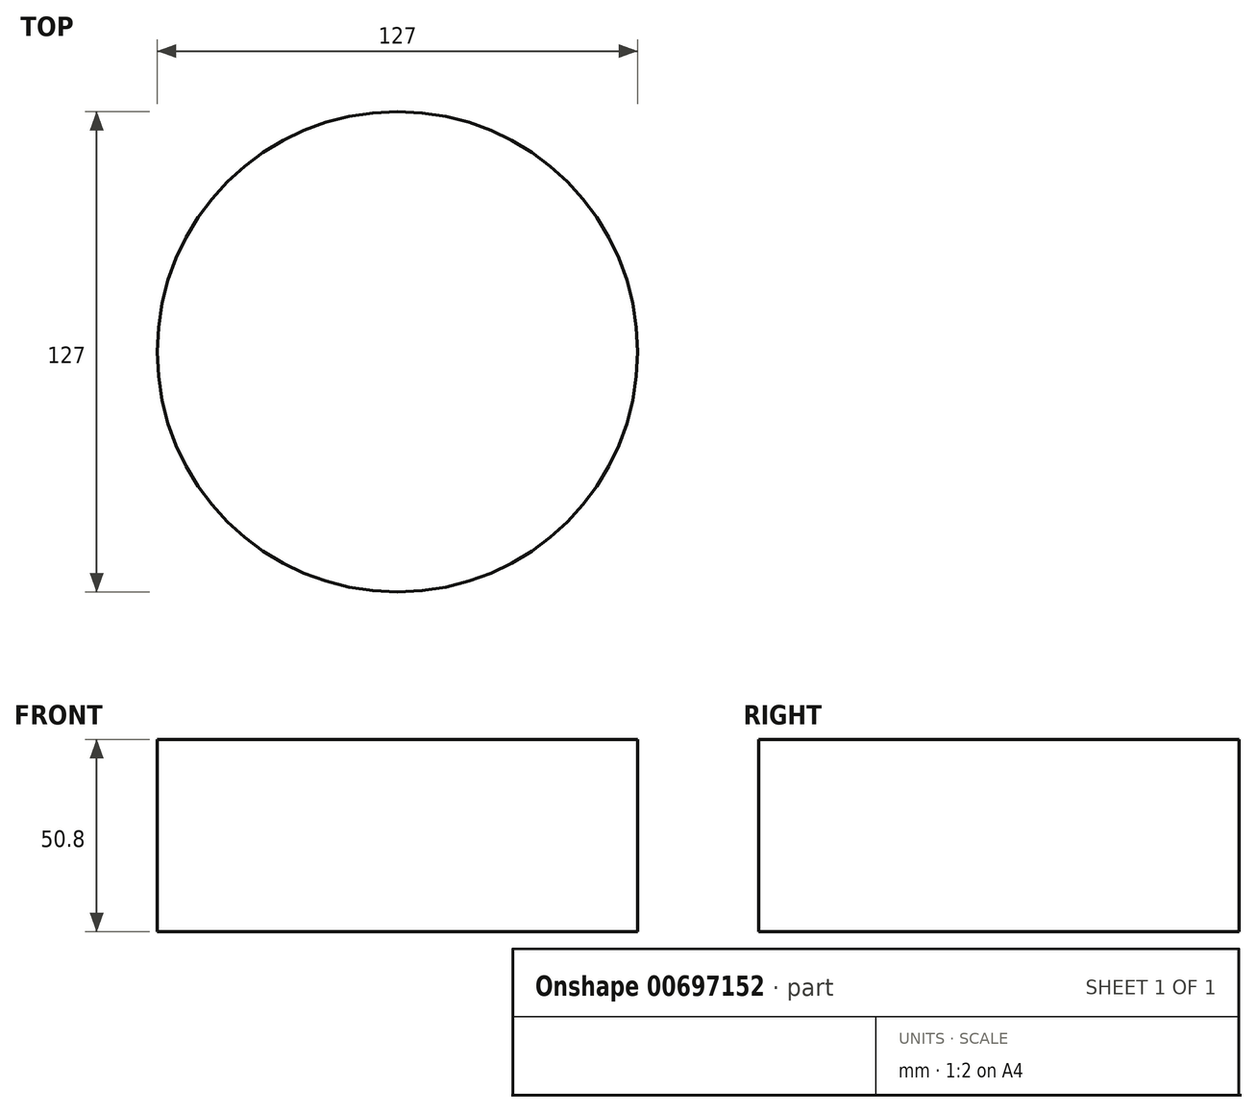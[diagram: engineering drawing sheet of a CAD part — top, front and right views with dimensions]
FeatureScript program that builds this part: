
annotation { "Feature Type Name" : "Feature", "Feature Type Description" : "" }
export const myFeature = defineFeature(function(context is Context, id is Id, definition is map)
    precondition{}
    {
        {
            var Q0;
            Q0=qCreatedBy(makeId("Top.planeOp"),FACE);
            var sketch = newSketch(context, id + "F0", { "sketchPlane" : qUnion([Q0])});
            skCircle(sketch, "E0", {"center": v(0, 0) * mm, "radius": 63.5 * mm});
            skSolve(sketch);
        }
        {
            var Q0;
            Q0 = qSketchRegion(id + "F0", true);
            extrude(context, id + "F1", {"entities" : qUnion([Q0]), "depth" : 50.8 * mm, "offsetDistance" : 25.4 * mm});
        }
    });
